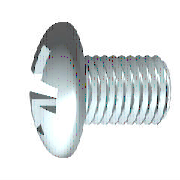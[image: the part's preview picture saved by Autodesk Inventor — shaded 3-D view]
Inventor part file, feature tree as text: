
AUTODESK INVENTOR PART (.ipt)
format: ipt  version: 2020 (Build 240168000, 168)  size: 264,704 bytes
history: native  units: mm (DEFAULTED — no unit token found)
features: other x2, plane x2, extrude x1
ambient origin geometry x7: Origin, YZ Plane, XZ Plane, X Axis, Y Axis, Z Axis, Center Point
bodies: Solid1 (feature_tree)
feature tree (5):
  other  "Базовый элемент"
  plane  "Work Plane1"
  extrude  "Паз"  Depth=2.0mm
  other  "Вырез"
  plane  "Work Plane3"
